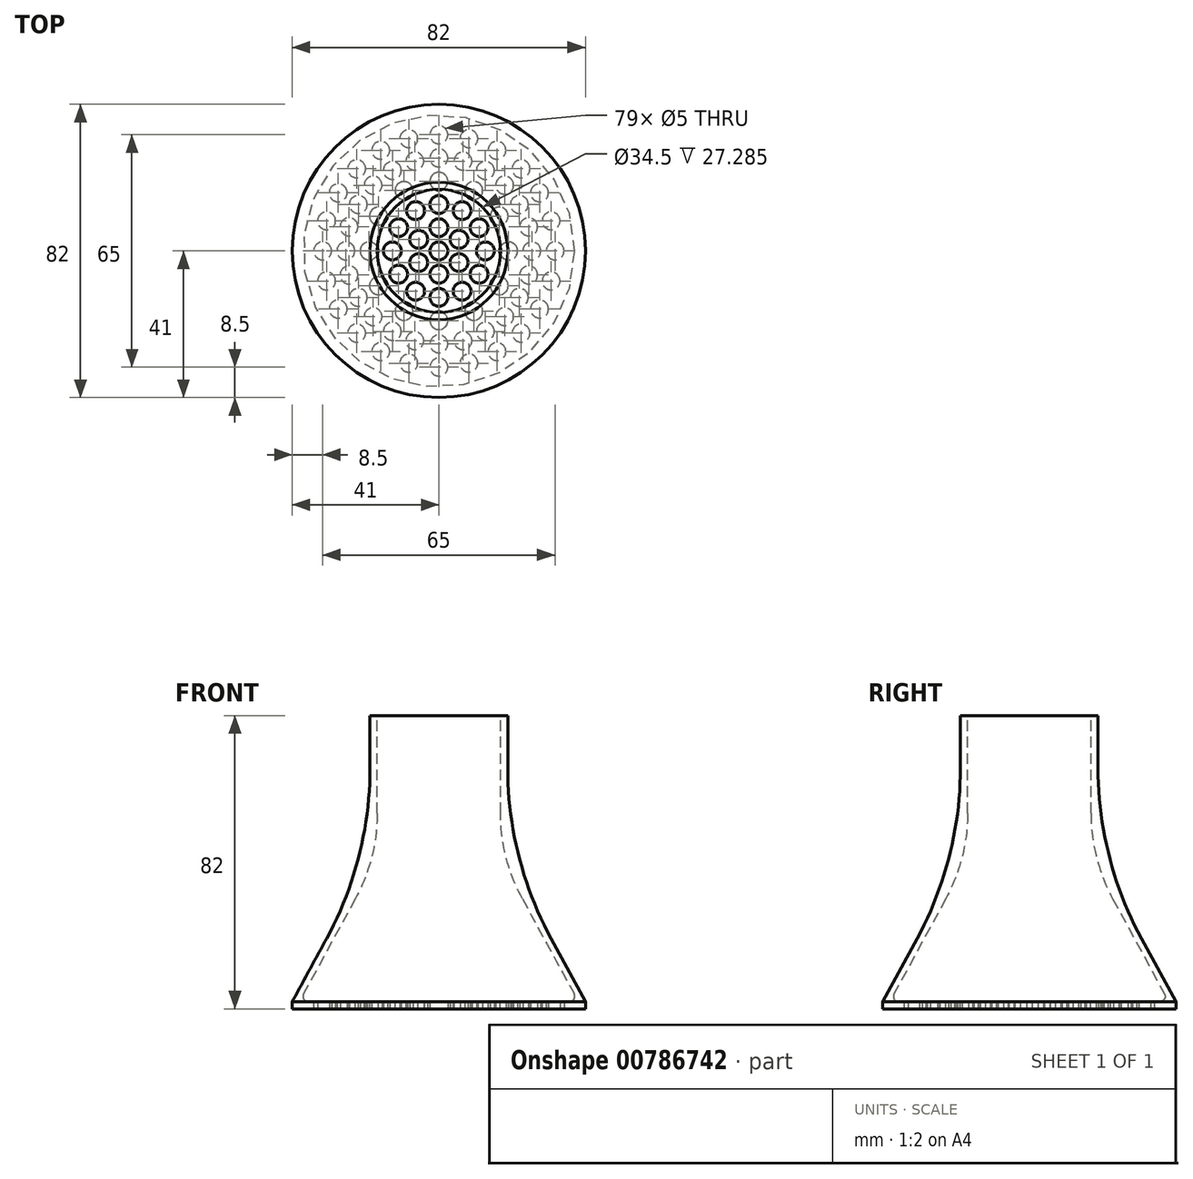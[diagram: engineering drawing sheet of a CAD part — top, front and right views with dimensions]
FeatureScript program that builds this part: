
annotation { "Feature Type Name" : "Feature", "Feature Type Description" : "" }
export const myFeature = defineFeature(function(context is Context, id is Id, definition is map)
    precondition{}
    {
        {
            var Q0;
            Q0=qCreatedBy(makeId("Front.planeOp"),FACE);
            var sketch = newSketch(context, id + "F0", { "sketchPlane" : qUnion([Q0])});
            skLineSegment(sketch, "E0", {"start": v(0, 0) * mm, "end": v(41, 0) * mm});
            skLineSegment(sketch, "E1", {"start": v(41, 0) * mm, "end": v(41, 2) * mm});
            skLineSegment(sketch, "E2", {"start": v(41, 2) * mm, "end": v(19.25, 42) * mm});
            skLineSegment(sketch, "E3", {"start": v(19.25, 42) * mm, "end": v(19.25, 82) * mm});
            skLineSegment(sketch, "E4", {"start": v(19.25, 82) * mm, "end": v(17.25, 82) * mm});
            skLineSegment(sketch, "E5", {"start": v(17.25, 82) * mm, "end": v(17.25, 42) * mm});
            skLineSegment(sketch, "E6", {"start": v(17.25, 42) * mm, "end": v(37.8, 4.22) * mm});
            skLineSegment(sketch, "E7", {"start": v(36.48, 2) * mm, "end": v(0, 2) * mm});
            skLineSegment(sketch, "E8", {"start": v(0, 2) * mm, "end": v(0, 0) * mm});
            skPoint(sketch, "E9.visualSharp", {"position": v(39, 2) * mm});
            skArc(sketch, "E9.filletArc", {"start": v(36.48, 2) * mm, "mid": v(37.77, 2.73) * mm, "end": v(37.8, 4.22) * mm});
            skSolve(sketch);
        }
        {
            var Q0;
            Q0 = qSketchRegion(id + "F0", true);
            var Q1;
            Q1=sQuery(id+"F0.wireOp",EDGE,"E8");
            revolve(context, id + "F1", {"surfaceOperationType" : NewSurfaceOperationType.NEW, "entities" : qUnion([Q0]), "axis" : qUnion([Q1]), "revolveType" : RevolveType.FULL});
        }
        {
            var Q0;
            Q0=makeQuery(id+"F1.opRevolve","SWEPT_EDGE",EDGE,{"disambiguationData":[OSD([sQuery(id+"F0.wireOp",EDGE,"E2"),sQuery(id+"F0.wireOp",EDGE,"E3")])]});
            fillet(context, id + "F2", {"entities" : qUnion([Q0]), "radius" : 100 * mm, "tangentPropagation" : true, "allowEdgeOverflow" : false});
        }
        {
            var Q0;
            Q0=makeQuery(id+"F1.opRevolve","SWEPT_EDGE",EDGE,{"disambiguationData":[OSD([sQuery(id+"F0.wireOp",EDGE,"E5"),sQuery(id+"F0.wireOp",EDGE,"E6")])]});
            fillet(context, id + "F3", {"entities" : qUnion([Q0]), "radius" : 50 * mm, "tangentPropagation" : true, "allowEdgeOverflow" : false});
        }
        {
            var Q0;
            Q0=makeQuery(id+"F1.opRevolve","SWEPT_FACE",FACE,{"disambiguationData":[OSD([sQuery(id+"F0.wireOp",EDGE,"E0")])]});
            var sketch = newSketch(context, id + "F4", { "sketchPlane" : qUnion([Q0])});
            skCircle(sketch, "E10", {"center": v(0, 0) * mm, "radius": 2.5 * mm});
            skCircle(sketch, "E11.0.1.0", {"center": v(0, 6.5) * mm, "radius": 2.5 * mm});
            skCircle(sketch, "E11.0.2.0", {"center": v(0, 13) * mm, "radius": 2.5 * mm});
            skCircle(sketch, "E11.0.3.0", {"center": v(0, 19.5) * mm, "radius": 2.5 * mm});
            skCircle(sketch, "E11.0.4.0", {"center": v(0, 26) * mm, "radius": 2.5 * mm});
            skCircle(sketch, "E11.0.5.0", {"center": v(0, 32.5) * mm, "radius": 2.5 * mm});
            skLineSegment(sketch, "E11.direction1", {"start": v(0, 0) * mm, "end": v(25, 0) * mm, "construction": true});
            skLineSegment(sketch, "E11.direction2", {"start": v(0, 0) * mm, "end": v(0, 6.5) * mm, "construction": true});
            skCircle(sketch, "E12.1.1", {"center": v(-5.63, 3.25) * mm, "radius": 2.5 * mm});
            skCircle(sketch, "E12.1.2", {"center": v(-11.26, 6.5) * mm, "radius": 2.5 * mm});
            skCircle(sketch, "E12.1.3", {"center": v(-16.89, 9.75) * mm, "radius": 2.5 * mm});
            skCircle(sketch, "E12.1.4", {"center": v(-22.52, 13) * mm, "radius": 2.5 * mm});
            skCircle(sketch, "E12.1.5", {"center": v(-28.15, 16.25) * mm, "radius": 2.5 * mm});
            skCircle(sketch, "E12.2.1", {"center": v(-5.63, -3.25) * mm, "radius": 2.5 * mm});
            skCircle(sketch, "E12.2.2", {"center": v(-11.26, -6.5) * mm, "radius": 2.5 * mm});
            skCircle(sketch, "E12.2.3", {"center": v(-16.89, -9.75) * mm, "radius": 2.5 * mm});
            skCircle(sketch, "E12.2.4", {"center": v(-22.52, -13) * mm, "radius": 2.5 * mm});
            skCircle(sketch, "E12.2.5", {"center": v(-28.15, -16.25) * mm, "radius": 2.5 * mm});
            skCircle(sketch, "E12.3.1", {"center": v(0, -6.5) * mm, "radius": 2.5 * mm});
            skCircle(sketch, "E12.3.2", {"center": v(0, -13) * mm, "radius": 2.5 * mm});
            skCircle(sketch, "E12.3.3", {"center": v(0, -19.5) * mm, "radius": 2.5 * mm});
            skCircle(sketch, "E12.3.4", {"center": v(0, -26) * mm, "radius": 2.5 * mm});
            skCircle(sketch, "E12.3.5", {"center": v(0, -32.5) * mm, "radius": 2.5 * mm});
            skCircle(sketch, "E12.4.1", {"center": v(5.63, -3.25) * mm, "radius": 2.5 * mm});
            skCircle(sketch, "E12.4.2", {"center": v(11.26, -6.5) * mm, "radius": 2.5 * mm});
            skCircle(sketch, "E12.4.3", {"center": v(16.89, -9.75) * mm, "radius": 2.5 * mm});
            skCircle(sketch, "E12.4.4", {"center": v(22.52, -13) * mm, "radius": 2.5 * mm});
            skCircle(sketch, "E12.4.5", {"center": v(28.15, -16.25) * mm, "radius": 2.5 * mm});
            skCircle(sketch, "E12.5.1", {"center": v(5.63, 3.25) * mm, "radius": 2.5 * mm});
            skCircle(sketch, "E12.5.2", {"center": v(11.26, 6.5) * mm, "radius": 2.5 * mm});
            skCircle(sketch, "E12.5.3", {"center": v(16.89, 9.75) * mm, "radius": 2.5 * mm});
            skCircle(sketch, "E12.5.4", {"center": v(22.52, 13) * mm, "radius": 2.5 * mm});
            skCircle(sketch, "E12.5.5", {"center": v(28.15, 16.25) * mm, "radius": 2.5 * mm});
            skCircle(sketch, "E13.1.1", {"center": v(-6.5, 11.26) * mm, "radius": 2.5 * mm});
            skCircle(sketch, "E13.1.2", {"center": v(-9.75, 16.89) * mm, "radius": 2.5 * mm});
            skCircle(sketch, "E13.1.3", {"center": v(-13, 22.52) * mm, "radius": 2.5 * mm});
            skCircle(sketch, "E13.1.4", {"center": v(-16.25, 28.15) * mm, "radius": 2.5 * mm});
            skCircle(sketch, "E13.3.1", {"center": v(-13, 0) * mm, "radius": 2.5 * mm});
            skCircle(sketch, "E13.3.2", {"center": v(-19.5, 0) * mm, "radius": 2.5 * mm});
            skCircle(sketch, "E13.3.3", {"center": v(-26, 0) * mm, "radius": 2.5 * mm});
            skCircle(sketch, "E13.3.4", {"center": v(-32.5, 0) * mm, "radius": 2.5 * mm});
            skCircle(sketch, "E13.5.1", {"center": v(-6.5, -11.26) * mm, "radius": 2.5 * mm});
            skCircle(sketch, "E13.5.2", {"center": v(-9.75, -16.89) * mm, "radius": 2.5 * mm});
            skCircle(sketch, "E13.5.3", {"center": v(-13, -22.52) * mm, "radius": 2.5 * mm});
            skCircle(sketch, "E13.5.4", {"center": v(-16.25, -28.15) * mm, "radius": 2.5 * mm});
            skCircle(sketch, "E13.7.1", {"center": v(6.5, -11.26) * mm, "radius": 2.5 * mm});
            skCircle(sketch, "E13.7.2", {"center": v(9.75, -16.89) * mm, "radius": 2.5 * mm});
            skCircle(sketch, "E13.7.3", {"center": v(13, -22.52) * mm, "radius": 2.5 * mm});
            skCircle(sketch, "E13.7.4", {"center": v(16.25, -28.15) * mm, "radius": 2.5 * mm});
            skCircle(sketch, "E13.9.1", {"center": v(13, 0) * mm, "radius": 2.5 * mm});
            skCircle(sketch, "E13.9.2", {"center": v(19.5, 0) * mm, "radius": 2.5 * mm});
            skCircle(sketch, "E13.9.3", {"center": v(26, 0) * mm, "radius": 2.5 * mm});
            skCircle(sketch, "E13.9.4", {"center": v(32.5, 0) * mm, "radius": 2.5 * mm});
            skCircle(sketch, "E13.11.1", {"center": v(6.5, 11.26) * mm, "radius": 2.5 * mm});
            skCircle(sketch, "E13.11.2", {"center": v(9.75, 16.89) * mm, "radius": 2.5 * mm});
            skCircle(sketch, "E13.11.3", {"center": v(13, 22.52) * mm, "radius": 2.5 * mm});
            skCircle(sketch, "E13.11.4", {"center": v(16.25, 28.15) * mm, "radius": 2.5 * mm});
            skCircle(sketch, "E14.1.0", {"center": v(-6.73, 25.11) * mm, "radius": 2.5 * mm});
            skCircle(sketch, "E14.1.1", {"center": v(-8.41, 31.4) * mm, "radius": 2.5 * mm});
            skCircle(sketch, "E14.3.0", {"center": v(-18.38, 18.38) * mm, "radius": 2.5 * mm});
            skCircle(sketch, "E14.3.1", {"center": v(-22.98, 22.98) * mm, "radius": 2.5 * mm});
            skCircle(sketch, "E14.5.0", {"center": v(-25.11, 6.73) * mm, "radius": 2.5 * mm});
            skCircle(sketch, "E14.5.1", {"center": v(-31.4, 8.41) * mm, "radius": 2.5 * mm});
            skCircle(sketch, "E14.7.0", {"center": v(-25.11, -6.73) * mm, "radius": 2.5 * mm});
            skCircle(sketch, "E14.7.1", {"center": v(-31.4, -8.41) * mm, "radius": 2.5 * mm});
            skCircle(sketch, "E14.9.0", {"center": v(-18.38, -18.38) * mm, "radius": 2.5 * mm});
            skCircle(sketch, "E14.9.1", {"center": v(-22.98, -22.98) * mm, "radius": 2.5 * mm});
            skCircle(sketch, "E14.11.0", {"center": v(-6.73, -25.11) * mm, "radius": 2.5 * mm});
            skCircle(sketch, "E14.11.1", {"center": v(-8.41, -31.4) * mm, "radius": 2.5 * mm});
            skCircle(sketch, "E14.13.0", {"center": v(6.73, -25.11) * mm, "radius": 2.5 * mm});
            skCircle(sketch, "E14.13.1", {"center": v(8.41, -31.4) * mm, "radius": 2.5 * mm});
            skCircle(sketch, "E14.15.0", {"center": v(18.38, -18.38) * mm, "radius": 2.5 * mm});
            skCircle(sketch, "E14.15.1", {"center": v(22.98, -22.98) * mm, "radius": 2.5 * mm});
            skCircle(sketch, "E14.17.0", {"center": v(25.11, -6.73) * mm, "radius": 2.5 * mm});
            skCircle(sketch, "E14.17.1", {"center": v(31.4, -8.41) * mm, "radius": 2.5 * mm});
            skCircle(sketch, "E14.19.0", {"center": v(25.11, 6.73) * mm, "radius": 2.5 * mm});
            skCircle(sketch, "E14.19.1", {"center": v(31.4, 8.41) * mm, "radius": 2.5 * mm});
            skCircle(sketch, "E14.21.0", {"center": v(18.38, 18.38) * mm, "radius": 2.5 * mm});
            skCircle(sketch, "E14.21.1", {"center": v(22.98, 22.98) * mm, "radius": 2.5 * mm});
            skCircle(sketch, "E14.23.0", {"center": v(6.73, 25.11) * mm, "radius": 2.5 * mm});
            skCircle(sketch, "E14.23.1", {"center": v(8.41, 31.4) * mm, "radius": 2.5 * mm});
            skSolve(sketch);
        }
        {
            var Q0;
            Q0 = qSketchRegion(id + "F4", true);
            var Q1;
            Q1=makeQuery(id+"F1.opRevolve","SWEPT_FACE",FACE,{"disambiguationData":[OSD([sQuery(id+"F0.wireOp",EDGE,"E7")])]});
            extrude(context, id + "F5", {"entities" : qUnion([Q0]), "operationType" : NewBodyOperationType.REMOVE, "endBound" : BoundingType.UP_TO_SURFACE, "oppositeDirection" : true, "depth" : 25 * mm, "endBoundEntityFace" : qUnion([Q1]), "offsetDistance" : 25 * mm});
        }
    });
